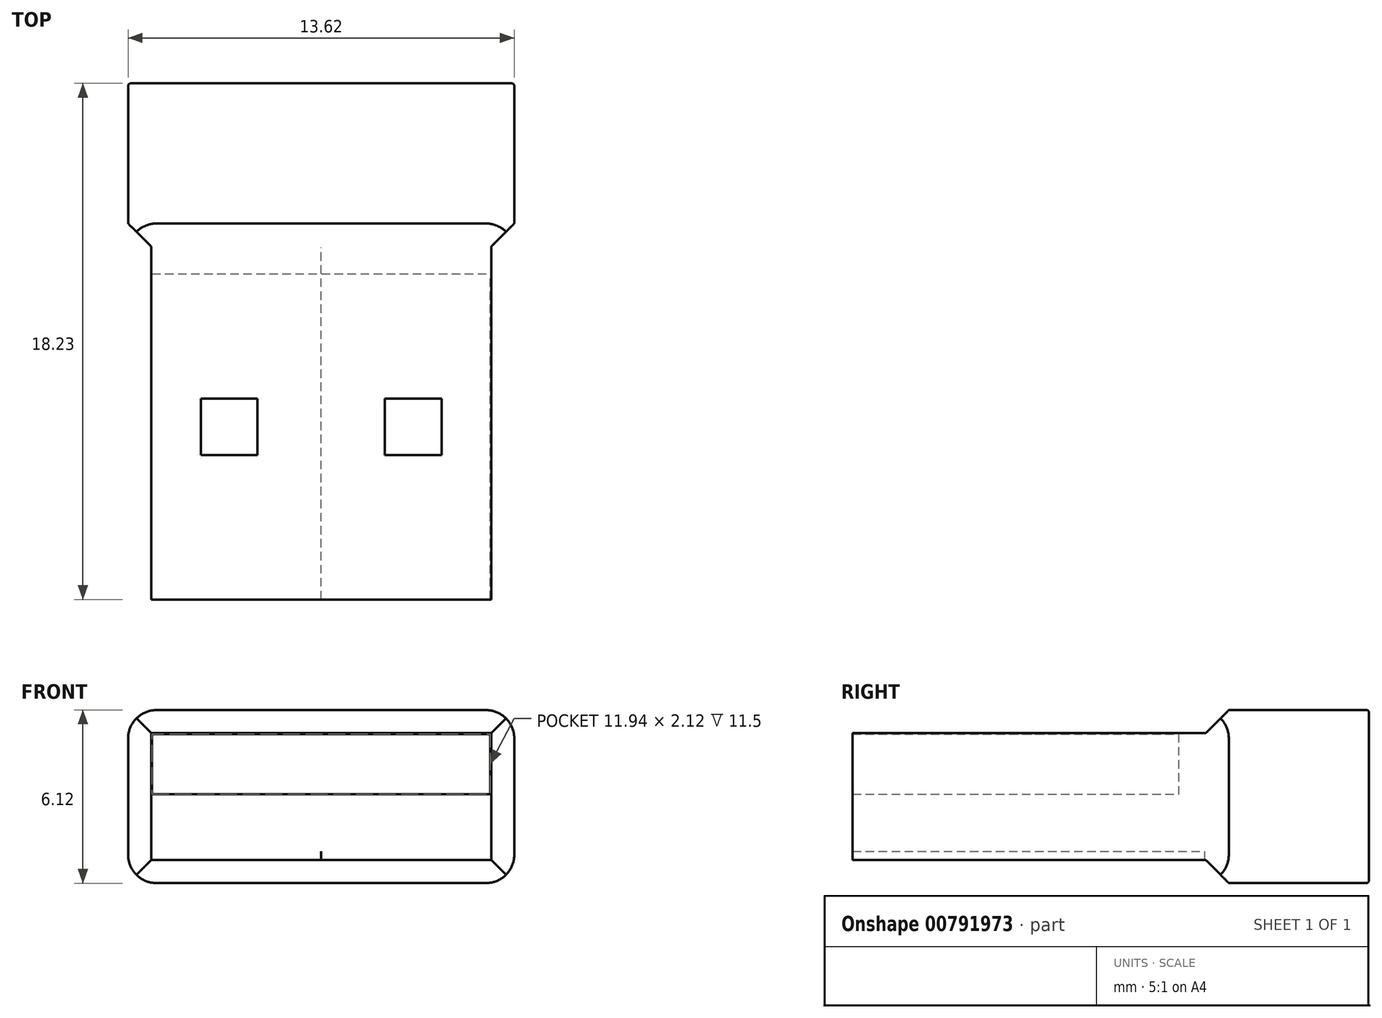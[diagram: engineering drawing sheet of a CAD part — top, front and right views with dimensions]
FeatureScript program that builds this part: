
annotation { "Feature Type Name" : "Feature", "Feature Type Description" : "" }
export const myFeature = defineFeature(function(context is Context, id is Id, definition is map)
    precondition{}
    {
        {
            var Q0;
            Q0=qCreatedBy(makeId("Front.planeOp"),FACE);
            var sketch = newSketch(context, id + "F0", { "sketchPlane" : qUnion([Q0])});
            skLineSegment(sketch, "E0.bottom", {"start": v(-6, 2.24) * mm, "end": v(6, 2.24) * mm});
            skLineSegment(sketch, "E0.top", {"start": v(-6, -2.24) * mm, "end": v(6, -2.24) * mm});
            skLineSegment(sketch, "E0.left", {"start": v(-6, 2.24) * mm, "end": v(-6, -2.24) * mm});
            skLineSegment(sketch, "E0.right", {"start": v(6, 2.24) * mm, "end": v(6, -2.24) * mm});
            skPoint(sketch, "E0.middle", {"position": v(0, 0) * mm});
            skLineSegment(sketch, "E1.0", {"start": v(-5.97, -2.2) * mm, "end": v(5.97, -2.2) * mm});
            skLineSegment(sketch, "E1.1", {"start": v(-5.97, 2.2) * mm, "end": v(-5.97, -2.2) * mm});
            skLineSegment(sketch, "E1.2", {"start": v(-5.97, 2.2) * mm, "end": v(5.97, 2.2) * mm});
            skLineSegment(sketch, "E1.3", {"start": v(5.97, 2.2) * mm, "end": v(5.97, -2.2) * mm});
            skLineSegment(sketch, "E2.0", {"start": v(-5.97, 0.1) * mm, "end": v(5.97, 0.1) * mm});
            skSolve(sketch);
        }
        {
            var Q0;
            Q0=makeQuery(id+"F0.imprint","IMPRINT",FACE,{"disambiguationData":[TD([[makeQuery(id+"F0.imprint","IMPRINT",EDGE,{"derivedFrom":sQuery(id+"F0.wireOp",EDGE,"E0.bottom")}),-1.0]])]});
            extrude(context, id + "F1", {"entities" : qUnion([Q0]), "endBound" : BoundingType.SYMMETRIC, "depth" : 11.5 * mm, "offsetDistance" : 25 * mm});
        }
        {
            var Q0;
            {var subQ0=sQuery(id+"F0.wireOp",EDGE,"E1.0");Q0=makeQuery(id+"F0.imprint","IMPRINT",FACE,{"disambiguationData":[TD([[makeQuery(id+"F0.imprint","IMPRINT",EDGE,{"derivedFrom":subQ0}),1.0]])]});}
            extrude(context, id + "F2", {"entities" : qUnion([Q0]), "operationType" : NewBodyOperationType.ADD, "endBound" : BoundingType.SYMMETRIC, "depth" : 11.5 * mm, "offsetDistance" : 25 * mm});
        }
        {
            var Q0;
            {var subQ0=sQuery(id+"F0.wireOp",EDGE,"E1.3");var subQ1=sQuery(id+"F0.wireOp",EDGE,"E1.1");var subQ2=sQuery(id+"F0.wireOp",EDGE,"E1.0");Q0=makeQuery(id+"F2.boolean.opBoolean","MERGE",FACE,{"derivedFrom":[makeQuery(id+"F1.opExtrude","CAP_FACE",FACE,{"disambiguationData":[OSD([sQuery(id+"F0.wireOp",EDGE,"E0.bottom"),sQuery(id+"F0.wireOp",EDGE,"E0.top"),sQuery(id+"F0.wireOp",EDGE,"E0.left"),sQuery(id+"F0.wireOp",EDGE,"E0.right"),subQ2,subQ1,sQuery(id+"F0.wireOp",EDGE,"E1.2"),subQ0])],"isStart":true}),makeQuery(id+"F2.opExtrude","CAP_FACE",FACE,{"disambiguationData":[OSD([subQ2,subQ1,subQ0,sQuery(id+"F0.wireOp",EDGE,"E2.0")])],"isStart":true})]});}
            var sketch = newSketch(context, id + "F3", { "sketchPlane" : qUnion([Q0])});
            skLineSegment(sketch, "E3.bottom", {"start": v(6.82, -3.06) * mm, "end": v(-6.82, -3.06) * mm});
            skLineSegment(sketch, "E3.top", {"start": v(6.82, 3.06) * mm, "end": v(-6.82, 3.06) * mm});
            skLineSegment(sketch, "E3.left", {"start": v(6.82, -3.06) * mm, "end": v(6.82, 3.06) * mm});
            skLineSegment(sketch, "E3.right", {"start": v(-6.82, -3.06) * mm, "end": v(-6.82, 3.06) * mm});
            skPoint(sketch, "E3.middle", {"position": v(0, 0) * mm});
            skSolve(sketch);
        }
        {
            var Q0;
            Q0=makeQuery(id+"F3.imprint","IMPRINT",FACE,{"disambiguationData":[TD([[makeQuery(id+"F3.imprint","IMPRINT",EDGE,{"derivedFrom":sQuery(id+"F3.wireOp",EDGE,"E3.bottom")}),-1.0]])]});
            var Q1;
            Q1=makeQuery(id+"F3.imprint","IMPRINT",FACE,{"disambiguationData":[TD([[makeQuery(id+"F3.imprint","IMPRINT",EDGE,{"derivedFrom":makeQuery(id+"F1.opExtrude","CAP_EDGE",EDGE,{"disambiguationData":[OSD([sQuery(id+"F0.wireOp",EDGE,"E0.bottom")])],"isStart":true})}),1.0]])]});
            var Q2;
            Q2=makeQuery(id+"F3.imprint","IMPRINT",FACE,{"disambiguationData":[TD([[makeQuery(id+"F3.imprint","IMPRINT",EDGE,{"derivedFrom":makeQuery(id+"F1.opExtrude","CAP_EDGE",EDGE,{"disambiguationData":[OSD([sQuery(id+"F0.wireOp",EDGE,"E1.2")])],"isStart":true})}),1.0]])]});
            extrude(context, id + "F4", {"entities" : qUnion([Q0, Q1, Q2]), "operationType" : NewBodyOperationType.ADD, "depth" : 6.73 * mm, "offsetDistance" : 25 * mm});
        }
        {
            var Q0;
            Q0=makeQuery(id+"F4.opExtrude","CAP_EDGE",EDGE,{"disambiguationData":[OSD([sQuery(id+"F3.wireOp",EDGE,"E3.top")])],"isStart":true});
            var Q1;
            Q1=makeQuery(id+"F4.opExtrude","CAP_EDGE",EDGE,{"disambiguationData":[OSD([sQuery(id+"F3.wireOp",EDGE,"E3.right")])],"isStart":true});
            var Q2;
            Q2=makeQuery(id+"F4.opExtrude","CAP_EDGE",EDGE,{"disambiguationData":[OSD([sQuery(id+"F3.wireOp",EDGE,"E3.bottom")])],"isStart":true});
            var Q3;
            Q3=makeQuery(id+"F4.opExtrude","CAP_EDGE",EDGE,{"disambiguationData":[OSD([sQuery(id+"F3.wireOp",EDGE,"E3.left")])],"isStart":true});
            chamfer(context, id + "F5", {"entities" : qUnion([Q0, Q1, Q2, Q3]), "width" : 1.78 * mm, "tangentPropagation" : true});
        }
        {
            var Q0;
            Q0=makeQuery(id+"F5.opChamfer","BLEND_EDGE",EDGE,{"blendedFrom":[makeQuery(id+"F4.opExtrude","CAP_EDGE",EDGE,{"disambiguationData":[OSD([sQuery(id+"F3.wireOp",EDGE,"E3.top")])],"isStart":true}),makeQuery(id+"F1.opExtrude","SWEPT_FACE",FACE,{"disambiguationData":[OSD([sQuery(id+"F0.wireOp",EDGE,"E0.bottom")])]})],"blendedInto":[makeQuery(id+"F1.opExtrude","SWEPT_FACE",FACE,{"disambiguationData":[OSD([sQuery(id+"F0.wireOp",EDGE,"E0.bottom")])]})]});
            var Q1;
            Q1=makeQuery(id+"F5.opChamfer","BLEND_EDGE",EDGE,{"blendedFrom":[makeQuery(id+"F4.opExtrude","CAP_EDGE",EDGE,{"disambiguationData":[OSD([sQuery(id+"F3.wireOp",EDGE,"E3.right")])],"isStart":true}),makeQuery(id+"F1.opExtrude","SWEPT_FACE",FACE,{"disambiguationData":[OSD([sQuery(id+"F0.wireOp",EDGE,"E0.right")])]})],"blendedInto":[makeQuery(id+"F1.opExtrude","SWEPT_FACE",FACE,{"disambiguationData":[OSD([sQuery(id+"F0.wireOp",EDGE,"E0.right")])]})]});
            var Q2;
            Q2=makeQuery(id+"F5.opChamfer","BLEND_EDGE",EDGE,{"blendedFrom":[makeQuery(id+"F4.opExtrude","CAP_EDGE",EDGE,{"disambiguationData":[OSD([sQuery(id+"F3.wireOp",EDGE,"E3.left")])],"isStart":true}),makeQuery(id+"F1.opExtrude","SWEPT_FACE",FACE,{"disambiguationData":[OSD([sQuery(id+"F0.wireOp",EDGE,"E0.left")])]})],"blendedInto":[makeQuery(id+"F1.opExtrude","SWEPT_FACE",FACE,{"disambiguationData":[OSD([sQuery(id+"F0.wireOp",EDGE,"E0.left")])]})]});
            var Q3;
            Q3=makeQuery(id+"F5.opChamfer","BLEND_EDGE",EDGE,{"blendedFrom":[makeQuery(id+"F4.opExtrude","CAP_EDGE",EDGE,{"disambiguationData":[OSD([sQuery(id+"F3.wireOp",EDGE,"E3.bottom")])],"isStart":true}),makeQuery(id+"F1.opExtrude","SWEPT_FACE",FACE,{"disambiguationData":[OSD([sQuery(id+"F0.wireOp",EDGE,"E0.top")])]})],"blendedInto":[makeQuery(id+"F1.opExtrude","SWEPT_FACE",FACE,{"disambiguationData":[OSD([sQuery(id+"F0.wireOp",EDGE,"E0.top")])]})]});
            fillet(context, id + "F6", {"entities" : qUnion([Q0, Q1, Q2, Q3]), "radius" : 0.1 * mm, "tangentPropagation" : true, "allowEdgeOverflow" : false});
        }
        {
            var Q0;
            Q0=makeQuery(id+"F4.opExtrude","SWEPT_EDGE",EDGE,{"disambiguationData":[OSD([sQuery(id+"F3.wireOp",EDGE,"E3.bottom"),sQuery(id+"F3.wireOp",EDGE,"E3.left")])]});
            var Q1;
            Q1=makeQuery(id+"F4.opExtrude","SWEPT_EDGE",EDGE,{"disambiguationData":[OSD([sQuery(id+"F3.wireOp",EDGE,"E3.top"),sQuery(id+"F3.wireOp",EDGE,"E3.left")])]});
            var Q2;
            Q2=makeQuery(id+"F4.opExtrude","SWEPT_EDGE",EDGE,{"disambiguationData":[OSD([sQuery(id+"F3.wireOp",EDGE,"E3.bottom"),sQuery(id+"F3.wireOp",EDGE,"E3.right")])]});
            var Q3;
            Q3=makeQuery(id+"F4.opExtrude","SWEPT_EDGE",EDGE,{"disambiguationData":[OSD([sQuery(id+"F3.wireOp",EDGE,"E3.top"),sQuery(id+"F3.wireOp",EDGE,"E3.right")])]});
            fillet(context, id + "F7", {"entities" : qUnion([Q0, Q1, Q2, Q3]), "radius" : 1 * mm, "tangentPropagation" : true, "allowEdgeOverflow" : false});
        }
        {
            var Q0;
            Q0=makeQuery(id+"F4.opExtrude","CAP_EDGE",EDGE,{"disambiguationData":[OSD([sQuery(id+"F3.wireOp",EDGE,"E3.top")])],"isStart":false});
            fillet(context, id + "F8", {"entities" : qUnion([Q0]), "radius" : 0.1 * mm, "tangentPropagation" : true, "allowEdgeOverflow" : false});
        }
        {
            var Q0;
            Q0=makeQuery(id+"F1.opExtrude","SWEPT_FACE",FACE,{"disambiguationData":[OSD([sQuery(id+"F0.wireOp",EDGE,"E0.bottom")])]});
            var sketch = newSketch(context, id + "F9", { "sketchPlane" : qUnion([Q0])});
            skLineSegment(sketch, "E4.bottom", {"start": v(-2.25, -0.65) * mm, "end": v(-4.25, -0.65) * mm});
            skLineSegment(sketch, "E4.top", {"start": v(-2.25, 1.35) * mm, "end": v(-4.25, 1.35) * mm});
            skLineSegment(sketch, "E4.left", {"start": v(-2.25, -0.65) * mm, "end": v(-2.25, 1.35) * mm});
            skLineSegment(sketch, "E4.right", {"start": v(-4.25, -0.65) * mm, "end": v(-4.25, 1.35) * mm});
            skPoint(sketch, "E4.middle", {"position": v(-3.25, 0.35) * mm});
            skLineSegment(sketch, "E5.MirrorCS", {"start": v(2.25, -0.65) * mm, "end": v(4.25, -0.65) * mm});
            skLineSegment(sketch, "E6.MirrorCS", {"start": v(4.25, -0.65) * mm, "end": v(4.25, 1.35) * mm});
            skLineSegment(sketch, "E7.MirrorCS", {"start": v(2.25, 1.35) * mm, "end": v(4.25, 1.35) * mm});
            skLineSegment(sketch, "E8.MirrorCS", {"start": v(2.25, -0.65) * mm, "end": v(2.25, 1.35) * mm});
            skSolve(sketch);
        }
        {
            var Q0;
            Q0=makeQuery(id+"F9.imprint","IMPRINT",FACE,{"disambiguationData":[TD([[makeQuery(id+"F9.imprint","IMPRINT",EDGE,{"derivedFrom":sQuery(id+"F9.wireOp",EDGE,"E4.bottom")}),-1.0]])]});
            var Q1;
            Q1=makeQuery(id+"F9.imprint","IMPRINT",FACE,{"disambiguationData":[TD([[makeQuery(id+"F9.imprint","IMPRINT",EDGE,{"derivedFrom":sQuery(id+"F9.wireOp",EDGE,"E5.MirrorCS")}),1.0]])]});
            var Q2;
            Q2=makeQuery(id+"F2.opExtrude","SWEPT_FACE",FACE,{"disambiguationData":[OSD([sQuery(id+"F0.wireOp",EDGE,"E2.0")])]});
            extrude(context, id + "F10", {"entities" : qUnion([Q0, Q1]), "operationType" : NewBodyOperationType.REMOVE, "endBound" : BoundingType.UP_TO_SURFACE, "oppositeDirection" : true, "depth" : 25 * mm, "endBoundEntityFace" : qUnion([Q2]), "offsetDistance" : 25 * mm});
        }
        {
            var Q0;
            Q0=makeQuery(id+"F1.opExtrude","SWEPT_FACE",FACE,{"disambiguationData":[OSD([sQuery(id+"F0.wireOp",EDGE,"E0.top")])]});
            var sketch = newSketch(context, id + "F11", { "sketchPlane" : qUnion([Q0])});
            skLineSegment(sketch, "E9", {"start": v(0, 5.75) * mm, "end": v(0, -6.67) * mm});
            skSolve(sketch);
        }
        {
            var Q0;
            {var subQ0=sQuery(id+"F11.wireOp",EDGE,"E9");Q0=makeQuery(id+"F11.imprint","IMPRINT",FACE,{"disambiguationData":[TD([[makeQuery(id+"F11.imprint","IMPRINT",EDGE,{"derivedFrom":subQ0}),-1.0]])]});}
            var Q1;
            {var subQ0=sQuery(id+"F11.wireOp",EDGE,"E9");Q1=makeQuery(id+"F11.imprint","IMPRINT",FACE,{"disambiguationData":[TD([[makeQuery(id+"F11.imprint","IMPRINT",EDGE,{"derivedFrom":subQ0}),1.0]])]});}
            extrude(context, id + "F12", {"entities" : qUnion([Q0, Q1]), "operationType" : NewBodyOperationType.REMOVE, "oppositeDirection" : true, "depth" : 0.3 * mm, "offsetDistance" : 25 * mm});
        }
    });
